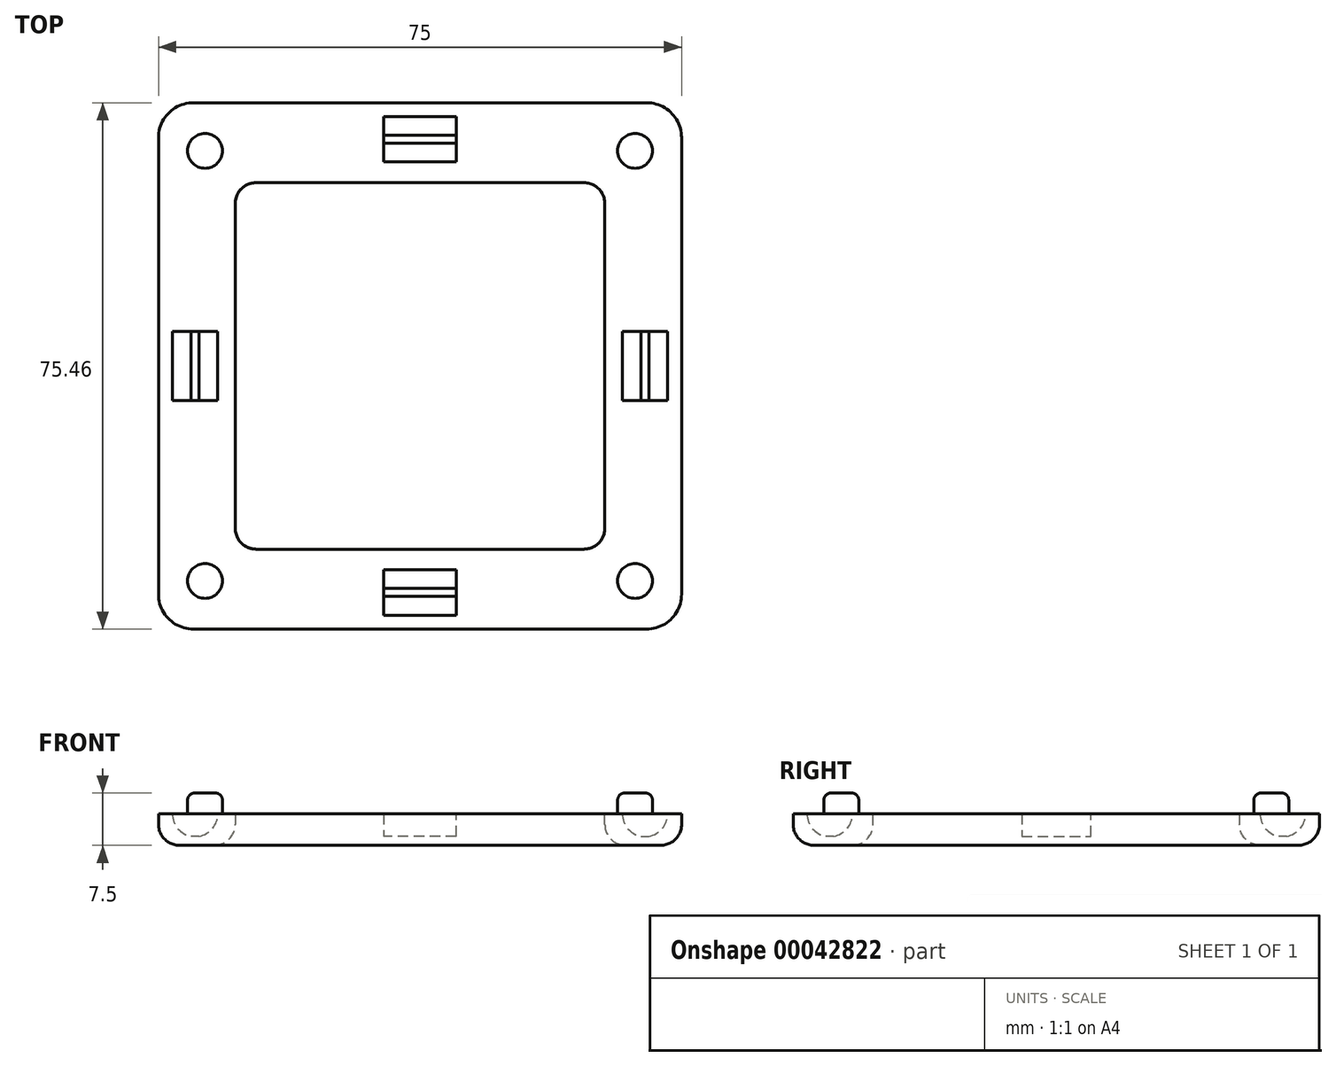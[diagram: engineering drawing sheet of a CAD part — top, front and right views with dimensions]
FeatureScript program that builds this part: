
annotation { "Feature Type Name" : "Feature", "Feature Type Description" : "" }
export const myFeature = defineFeature(function(context is Context, id is Id, definition is map)
    precondition{}
    {
        {
            var Q0;
            Q0=qCreatedBy(makeId("Top.planeOp"),FACE);
            var sketch = newSketch(context, id + "F0", { "sketchPlane" : qUnion([Q0])});
            skLineSegment(sketch, "E0", {"start": v(0, 37.27) * mm, "end": v(37.5, 37.27) * mm});
            skLineSegment(sketch, "E1", {"start": v(-37.5, 37.27) * mm, "end": v(0, 37.27) * mm});
            skLineSegment(sketch, "E2", {"start": v(-37.5, 37.27) * mm, "end": v(-37.5, -37.73) * mm});
            skLineSegment(sketch, "E3", {"start": v(-37.5, -37.73) * mm, "end": v(37.5, -37.73) * mm});
            skLineSegment(sketch, "E4", {"start": v(37.5, 37.27) * mm, "end": v(37.5, -0.23) * mm});
            skLineSegment(sketch, "E5", {"start": v(37.5, -0.23) * mm, "end": v(37.5, -37.73) * mm});
            skLineSegment(sketch, "E6", {"start": v(0, 26.27) * mm, "end": v(26.5, 26.27) * mm});
            skLineSegment(sketch, "E7", {"start": v(26.5, 26.27) * mm, "end": v(26.5, -26.73) * mm});
            skLineSegment(sketch, "E8", {"start": v(26.5, -26.73) * mm, "end": v(0, -26.73) * mm});
            skLineSegment(sketch, "E9", {"start": v(0, -26.73) * mm, "end": v(-26.5, -26.73) * mm});
            skLineSegment(sketch, "E10", {"start": v(-26.5, 26.27) * mm, "end": v(-26.5, 26.27) * mm});
            skLineSegment(sketch, "E11", {"start": v(0, 26.27) * mm, "end": v(-26.5, 26.27) * mm});
            skLineSegment(sketch, "E12", {"start": v(-26.5, 26.27) * mm, "end": v(-26.5, 0) * mm});
            skLineSegment(sketch, "E13", {"start": v(-26.5, -26.73) * mm, "end": v(-26.5, 0) * mm});
            skLineSegment(sketch, "E14", {"start": v(0, 0) * mm, "end": v(0, 26.27) * mm});
            skLineSegment(sketch, "E15", {"start": v(0, 0) * mm, "end": v(0, -26.73) * mm});
            skLineSegment(sketch, "E16", {"start": v(-26.5, 0) * mm, "end": v(0, 0) * mm});
            skLineSegment(sketch, "E17", {"start": v(0, 0) * mm, "end": v(26.5, -0.23) * mm});
            skLineSegment(sketch, "E18", {"start": v(0, -35.73) * mm, "end": v(5.2, -35.73) * mm});
            skLineSegment(sketch, "E19", {"start": v(-5.2, -35.73) * mm, "end": v(0, -35.73) * mm});
            skLineSegment(sketch, "E20", {"start": v(-5.2, -29.23) * mm, "end": v(-5.2, -35.73) * mm});
            skLineSegment(sketch, "E21", {"start": v(-5.2, -29.23) * mm, "end": v(5.2, -29.23) * mm});
            skLineSegment(sketch, "E22", {"start": v(5.2, -29.23) * mm, "end": v(5.2, -35.73) * mm});
            skLineSegment(sketch, "E23.MirrorCS", {"start": v(0, 35.73) * mm, "end": v(5.2, 35.73) * mm});
            skLineSegment(sketch, "E24.MirrorCS", {"start": v(-5.2, 29.23) * mm, "end": v(-5.2, 35.73) * mm});
            skLineSegment(sketch, "E25.MirrorCS", {"start": v(-5.2, 29.23) * mm, "end": v(5.2, 29.23) * mm});
            skLineSegment(sketch, "E26", {"start": v(5.2, 35.73) * mm, "end": v(5.2, 29.23) * mm});
            skLineSegment(sketch, "E27", {"start": v(0, 35.73) * mm, "end": v(-5.2, 35.73) * mm});
            skLineSegment(sketch, "E28", {"start": v(35.5, -0.23) * mm, "end": v(35.5, -5.43) * mm});
            skLineSegment(sketch, "E29", {"start": v(35.5, -5.43) * mm, "end": v(29, -5.43) * mm});
            skLineSegment(sketch, "E30", {"start": v(29, -5.43) * mm, "end": v(29, 4.97) * mm});
            skLineSegment(sketch, "E31", {"start": v(29, 4.97) * mm, "end": v(35.5, 4.97) * mm});
            skLineSegment(sketch, "E32", {"start": v(35.5, 4.97) * mm, "end": v(35.5, -0.23) * mm});
            skLineSegment(sketch, "E33.MirrorCS", {"start": v(-29, 4.97) * mm, "end": v(-35.5, 4.97) * mm});
            skLineSegment(sketch, "E34.MirrorCS", {"start": v(-29, -5.43) * mm, "end": v(-29, 4.97) * mm});
            skLineSegment(sketch, "E35.MirrorCS", {"start": v(-35.5, -5.43) * mm, "end": v(-29, -5.43) * mm});
            skLineSegment(sketch, "E36.MirrorCS", {"start": v(-35.5, -0.23) * mm, "end": v(-35.5, -5.43) * mm});
            skLineSegment(sketch, "E37.MirrorCS", {"start": v(-35.5, 4.97) * mm, "end": v(-35.5, -0.23) * mm});
            skSolve(sketch);
        }
        {
            var Q0;
            Q0=makeQuery(id+"F0.imprint","IMPRINT",FACE,{"disambiguationData":[TD([[makeQuery(id+"F0.imprint","IMPRINT",EDGE,{"derivedFrom":sQuery(id+"F0.wireOp",EDGE,"E18")}),1.0]])]});
            var Q1;
            Q1=makeQuery(id+"F0.imprint","IMPRINT",FACE,{"disambiguationData":[TD([[makeQuery(id+"F0.imprint","IMPRINT",EDGE,{"derivedFrom":sQuery(id+"F0.wireOp",EDGE,"E0")}),-1.0]])]});
            var Q2;
            {var subQ1=sQuery(id+"F0.wireOp",EDGE,"E8");Q2=makeQuery(id+"F0.imprint","IMPRINT",FACE,{"disambiguationData":[TD([[makeQuery(id+"F0.imprint","IMPRINT",EDGE,{"derivedFrom":subQ1}),-1.0]])]});}
            var Q3;
            Q3=makeQuery(id+"F0.imprint","IMPRINT",FACE,{"disambiguationData":[TD([[makeQuery(id+"F0.imprint","IMPRINT",EDGE,{"derivedFrom":sQuery(id+"F0.wireOp",EDGE,"E28")}),-1.0]])]});
            var Q4;
            Q4=makeQuery(id+"F0.imprint","IMPRINT",FACE,{"disambiguationData":[TD([[makeQuery(id+"F0.imprint","IMPRINT",EDGE,{"derivedFrom":sQuery(id+"F0.wireOp",EDGE,"E23.MirrorCS")}),-1.0]])]});
            var Q5;
            Q5=makeQuery(id+"F0.imprint","IMPRINT",FACE,{"disambiguationData":[TD([[makeQuery(id+"F0.imprint","IMPRINT",EDGE,{"derivedFrom":sQuery(id+"F0.wireOp",EDGE,"E9")}),-1.0]])]});
            var Q6;
            Q6=makeQuery(id+"F0.imprint","IMPRINT",FACE,{"disambiguationData":[TD([[makeQuery(id+"F0.imprint","IMPRINT",EDGE,{"derivedFrom":sQuery(id+"F0.wireOp",EDGE,"E11")}),1.0]])]});
            var Q7;
            {var subQ2=sQuery(id+"F0.wireOp",EDGE,"E6");Q7=makeQuery(id+"F0.imprint","IMPRINT",FACE,{"disambiguationData":[TD([[makeQuery(id+"F0.imprint","IMPRINT",EDGE,{"derivedFrom":subQ2}),-1.0]])]});}
            var Q8;
            Q8=makeQuery(id+"F0.imprint","IMPRINT",FACE,{"disambiguationData":[TD([[makeQuery(id+"F0.imprint","IMPRINT",EDGE,{"derivedFrom":sQuery(id+"F0.wireOp",EDGE,"E33.MirrorCS")}),1.0]])]});
            extrude(context, id + "F1", {"entities" : qUnion([Q0, Q1, Q2, Q3, Q4, Q5, Q6, Q7, Q8]), "oppositeDirection" : true, "depth" : 4.5 * mm});
        }
        {
            var Q0;
            {var subQ2=sQuery(id+"F0.wireOp",EDGE,"E6");Q0=makeQuery(id+"F0.imprint","IMPRINT",FACE,{"disambiguationData":[TD([[makeQuery(id+"F0.imprint","IMPRINT",EDGE,{"derivedFrom":subQ2}),-1.0]])]});}
            var Q1;
            {var subQ1=sQuery(id+"F0.wireOp",EDGE,"E8");Q1=makeQuery(id+"F0.imprint","IMPRINT",FACE,{"disambiguationData":[TD([[makeQuery(id+"F0.imprint","IMPRINT",EDGE,{"derivedFrom":subQ1}),-1.0]])]});}
            var Q2;
            Q2=makeQuery(id+"F0.imprint","IMPRINT",FACE,{"disambiguationData":[TD([[makeQuery(id+"F0.imprint","IMPRINT",EDGE,{"derivedFrom":sQuery(id+"F0.wireOp",EDGE,"E9")}),-1.0]])]});
            var Q3;
            Q3=makeQuery(id+"F0.imprint","IMPRINT",FACE,{"disambiguationData":[TD([[makeQuery(id+"F0.imprint","IMPRINT",EDGE,{"derivedFrom":sQuery(id+"F0.wireOp",EDGE,"E11")}),1.0]])]});
            extrude(context, id + "F2", {"entities" : qUnion([Q0, Q1, Q2, Q3]), "operationType" : NewBodyOperationType.REMOVE, "oppositeDirection" : true, "depth" : 5 * mm});
        }
        {
            var Q0;
            Q0=makeQuery(id+"F1.opExtrude","SWEPT_EDGE",EDGE,{"disambiguationData":[OSD([sQuery(id+"F0.wireOp",EDGE,"E3"),sQuery(id+"F0.wireOp",EDGE,"E5")])]});
            var Q1;
            Q1=makeQuery(id+"F1.opExtrude","SWEPT_EDGE",EDGE,{"disambiguationData":[OSD([sQuery(id+"F0.wireOp",EDGE,"E0"),sQuery(id+"F0.wireOp",EDGE,"E4")])]});
            var Q2;
            Q2=makeQuery(id+"F1.opExtrude","SWEPT_EDGE",EDGE,{"disambiguationData":[OSD([sQuery(id+"F0.wireOp",EDGE,"E2"),sQuery(id+"F0.wireOp",EDGE,"E3")])]});
            var Q3;
            Q3=makeQuery(id+"F1.opExtrude","SWEPT_EDGE",EDGE,{"disambiguationData":[OSD([sQuery(id+"F0.wireOp",EDGE,"E1"),sQuery(id+"F0.wireOp",EDGE,"E2")])]});
            fillet(context, id + "F3", {"entities" : qUnion([Q0, Q1, Q2, Q3]), "radius" : 5 * mm, "tangentPropagation" : true, "allowEdgeOverflow" : false});
        }
        {
            var Q0;
            Q0=makeQuery(id+"F2.boolean.opBoolean","COPY",EDGE,{"derivedFrom":makeQuery(id+"F2.opExtrude","SWEPT_EDGE",EDGE,{"disambiguationData":[OSD([sQuery(id+"F0.wireOp",EDGE,"E7"),sQuery(id+"F0.wireOp",EDGE,"E8")])]})});
            var Q1;
            Q1=makeQuery(id+"F2.boolean.opBoolean","COPY",EDGE,{"derivedFrom":makeQuery(id+"F2.opExtrude","SWEPT_EDGE",EDGE,{"disambiguationData":[OSD([sQuery(id+"F0.wireOp",EDGE,"E9"),sQuery(id+"F0.wireOp",EDGE,"E13")])]})});
            var Q2;
            Q2=makeQuery(id+"F2.boolean.opBoolean","COPY",EDGE,{"derivedFrom":makeQuery(id+"F2.opExtrude","SWEPT_EDGE",EDGE,{"disambiguationData":[OSD([sQuery(id+"F0.wireOp",EDGE,"E6"),sQuery(id+"F0.wireOp",EDGE,"E7")])]})});
            var Q3;
            Q3=makeQuery(id+"F2.boolean.opBoolean","COPY",EDGE,{"derivedFrom":makeQuery(id+"F2.opExtrude","SWEPT_EDGE",EDGE,{"disambiguationData":[OSD([sQuery(id+"F0.wireOp",EDGE,"E11"),sQuery(id+"F0.wireOp",EDGE,"E12")])]})});
            fillet(context, id + "F4", {"entities" : qUnion([Q0, Q1, Q2, Q3]), "radius" : 3 * mm, "tangentPropagation" : true, "allowEdgeOverflow" : false});
        }
        {
            var Q0;
            Q0=makeQuery(id+"F1.opExtrude","CAP_FACE",FACE,{"disambiguationData":[OSD([sQuery(id+"F0.wireOp",EDGE,"E0"),sQuery(id+"F0.wireOp",EDGE,"E1"),sQuery(id+"F0.wireOp",EDGE,"E2"),sQuery(id+"F0.wireOp",EDGE,"E3"),sQuery(id+"F0.wireOp",EDGE,"E4"),sQuery(id+"F0.wireOp",EDGE,"E5")])],"isStart":false});
            var Q1;
            Q1=makeQuery(id+"F1.opExtrude","CAP_EDGE",EDGE,{"disambiguationData":[OSD([sQuery(id+"F0.wireOp",EDGE,"E4"),sQuery(id+"F0.wireOp",EDGE,"E5")])],"isStart":false});
            var Q2;
            Q2=makeQuery(id+"F1.opExtrude","CAP_EDGE",EDGE,{"disambiguationData":[OSD([sQuery(id+"F0.wireOp",EDGE,"E2")])],"isStart":false});
            var Q3;
            {var subQ0=sQuery(id+"F0.wireOp",EDGE,"E2");var subQ1=sQuery(id+"F0.wireOp",EDGE,"E3");Q3=makeQuery(id+"F3.opFillet","BLEND_EDGE",EDGE,{"blendedFrom":[makeQuery(id+"F1.opExtrude","SWEPT_EDGE",EDGE,{"disambiguationData":[OSD([subQ0,subQ1])]}),makeQuery(id+"F1.opExtrude","CAP_FACE",FACE,{"disambiguationData":[OSD([sQuery(id+"F0.wireOp",EDGE,"E0"),sQuery(id+"F0.wireOp",EDGE,"E1"),subQ0,subQ1,sQuery(id+"F0.wireOp",EDGE,"E4"),sQuery(id+"F0.wireOp",EDGE,"E5")])],"isStart":false})],"blendedInto":[makeQuery(id+"F1.opExtrude","CAP_FACE",FACE,{"disambiguationData":[OSD([sQuery(id+"F0.wireOp",EDGE,"E0"),sQuery(id+"F0.wireOp",EDGE,"E1"),subQ0,subQ1,sQuery(id+"F0.wireOp",EDGE,"E4"),sQuery(id+"F0.wireOp",EDGE,"E5")])],"isStart":false})]});}
            var Q4;
            Q4=makeQuery(id+"F1.opExtrude","CAP_EDGE",EDGE,{"disambiguationData":[OSD([sQuery(id+"F0.wireOp",EDGE,"E3")])],"isStart":false});
            var Q5;
            Q5=makeQuery(id+"F1.opExtrude","CAP_EDGE",EDGE,{"disambiguationData":[OSD([sQuery(id+"F0.wireOp",EDGE,"E0"),sQuery(id+"F0.wireOp",EDGE,"E1")])],"isStart":false});
            var Q6;
            {var subQ0=sQuery(id+"F0.wireOp",EDGE,"E0");var subQ1=sQuery(id+"F0.wireOp",EDGE,"E4");Q6=makeQuery(id+"F3.opFillet","BLEND_EDGE",EDGE,{"blendedFrom":[makeQuery(id+"F1.opExtrude","SWEPT_EDGE",EDGE,{"disambiguationData":[OSD([subQ0,subQ1])]}),makeQuery(id+"F1.opExtrude","CAP_FACE",FACE,{"disambiguationData":[OSD([subQ0,sQuery(id+"F0.wireOp",EDGE,"E1"),sQuery(id+"F0.wireOp",EDGE,"E2"),sQuery(id+"F0.wireOp",EDGE,"E3"),subQ1,sQuery(id+"F0.wireOp",EDGE,"E5")])],"isStart":false})],"blendedInto":[makeQuery(id+"F1.opExtrude","CAP_FACE",FACE,{"disambiguationData":[OSD([subQ0,sQuery(id+"F0.wireOp",EDGE,"E1"),sQuery(id+"F0.wireOp",EDGE,"E2"),sQuery(id+"F0.wireOp",EDGE,"E3"),subQ1,sQuery(id+"F0.wireOp",EDGE,"E5")])],"isStart":false})]});}
            fillet(context, id + "F5", {"entities" : qUnion([Q0, Q1, Q2, Q3, Q4, Q5, Q6]), "radius" : 3 * mm, "allowEdgeOverflow" : false});
        }
        {
            var Q0;
            Q0=makeQuery(id+"F0.imprint","IMPRINT",FACE,{"disambiguationData":[TD([[makeQuery(id+"F0.imprint","IMPRINT",EDGE,{"derivedFrom":sQuery(id+"F0.wireOp",EDGE,"E18")}),1.0]])]});
            var Q1;
            Q1=makeQuery(id+"F0.imprint","IMPRINT",FACE,{"disambiguationData":[TD([[makeQuery(id+"F0.imprint","IMPRINT",EDGE,{"derivedFrom":sQuery(id+"F0.wireOp",EDGE,"E33.MirrorCS")}),1.0]])]});
            var Q2;
            Q2=makeQuery(id+"F0.imprint","IMPRINT",FACE,{"disambiguationData":[TD([[makeQuery(id+"F0.imprint","IMPRINT",EDGE,{"derivedFrom":sQuery(id+"F0.wireOp",EDGE,"E23.MirrorCS")}),-1.0]])]});
            var Q3;
            Q3=makeQuery(id+"F0.imprint","IMPRINT",FACE,{"disambiguationData":[TD([[makeQuery(id+"F0.imprint","IMPRINT",EDGE,{"derivedFrom":sQuery(id+"F0.wireOp",EDGE,"E28")}),-1.0]])]});
            extrude(context, id + "F6", {"entities" : qUnion([Q0, Q1, Q2, Q3]), "operationType" : NewBodyOperationType.REMOVE, "oppositeDirection" : true, "depth" : 3.2 * mm});
        }
        {
            var Q0;
            Q0=makeQuery(id+"F1.opExtrude","SWEPT_BODY",BODY,{"disambiguationData":[OSD([sQuery(id+"F0.wireOp",EDGE,"E0"),sQuery(id+"F0.wireOp",EDGE,"E1"),sQuery(id+"F0.wireOp",EDGE,"E2"),sQuery(id+"F0.wireOp",EDGE,"E3"),sQuery(id+"F0.wireOp",EDGE,"E4"),sQuery(id+"F0.wireOp",EDGE,"E5")])]});
            var Q1;
            Q1=qCreatedBy(makeId("Front.planeOp"),FACE);
            mirror(context, id + "F7", {"operationType" : NewBodyOperationType.ADD, "entities" : qUnion([Q0]), "mirrorPlane" : qUnion([Q1])});
        }
        {
            var Q0;
            Q0=makeQuery(id+"F6.boolean.opBoolean","COPY",FACE,{"derivedFrom":makeQuery(id+"F6.opExtrude","SWEPT_FACE",FACE,{"disambiguationData":[OSD([sQuery(id+"F0.wireOp",EDGE,"E33.MirrorCS")])]})});
            var sketch = newSketch(context, id + "F8", { "sketchPlane" : qUnion([Q0])});
            skArc(sketch, "E38", {"start": v(-35.5, 0) * mm, "mid": v(-32.25, -3.25) * mm, "end": v(-29, 0) * mm});
            skSolve(sketch);
        }
        {
            var Q0;
            {var subQ0=sQuery(id+"F0.wireOp",EDGE,"E33.MirrorCS");var subQ4=makeQuery(id+"F6.boolean.opBoolean","COPY",EDGE,{"derivedFrom":makeQuery(id+"F6.opExtrude","SWEPT_EDGE",EDGE,{"disambiguationData":[OSD([subQ0,sQuery(id+"F0.wireOp",EDGE,"E37.MirrorCS")])]})});Q0=makeQuery(id+"F8.imprint","IMPRINT",FACE,{"disambiguationData":[TD([[makeQuery(id+"F8.imprint","IMPRINT",EDGE,{"derivedFrom":subQ4}),-1.0]])]});}
            var Q1;
            {var subQ0=sQuery(id+"F0.wireOp",EDGE,"E33.MirrorCS");var subQ4=makeQuery(id+"F6.boolean.opBoolean","COPY",EDGE,{"derivedFrom":makeQuery(id+"F6.opExtrude","SWEPT_EDGE",EDGE,{"disambiguationData":[OSD([subQ0,sQuery(id+"F0.wireOp",EDGE,"E34.MirrorCS")])]})});Q1=makeQuery(id+"F8.imprint","IMPRINT",FACE,{"disambiguationData":[TD([[makeQuery(id+"F8.imprint","IMPRINT",EDGE,{"derivedFrom":subQ4}),1.0]])]});}
            extrude(context, id + "F9", {"entities" : qUnion([Q0, Q1]), "operationType" : NewBodyOperationType.ADD, "endBound" : BoundingType.UP_TO_NEXT, "depth" : 25 * mm});
        }
        {
            var Q0;
            Q0=makeQuery(id+"F1.opExtrude","SWEPT_BODY",BODY,{"disambiguationData":[OSD([sQuery(id+"F0.wireOp",EDGE,"E0"),sQuery(id+"F0.wireOp",EDGE,"E1"),sQuery(id+"F0.wireOp",EDGE,"E2"),sQuery(id+"F0.wireOp",EDGE,"E3"),sQuery(id+"F0.wireOp",EDGE,"E4"),sQuery(id+"F0.wireOp",EDGE,"E5")])]});
            var Q1;
            Q1=qCreatedBy(makeId("Right.planeOp"),FACE);
            mirror(context, id + "F10", {"operationType" : NewBodyOperationType.ADD, "entities" : qUnion([Q0]), "mirrorPlane" : qUnion([Q1])});
        }
        {
            var Q0;
            {var subQ0=makeQuery(id+"F1.opExtrude","CAP_FACE",FACE,{"disambiguationData":[OSD([sQuery(id+"F0.wireOp",EDGE,"E0"),sQuery(id+"F0.wireOp",EDGE,"E1"),sQuery(id+"F0.wireOp",EDGE,"E2"),sQuery(id+"F0.wireOp",EDGE,"E3"),sQuery(id+"F0.wireOp",EDGE,"E4"),sQuery(id+"F0.wireOp",EDGE,"E5")])],"isStart":true});Q0=makeQuery(id+"F7.boolean.opBoolean","MERGE",FACE,{"derivedFrom":[subQ0,makeQuery(id+"F7.opPattern","COPY",FACE,{"derivedFrom":subQ0,"instanceName":"1"})]});}
            var sketch = newSketch(context, id + "F11", { "sketchPlane" : qUnion([Q0])});
            skCircle(sketch, "E39", {"center": v(-30.83, 30.83) * mm, "radius": 2.5 * mm});
            skCircle(sketch, "E40", {"center": v(30.83, 30.83) * mm, "radius": 2.5 * mm});
            skCircle(sketch, "E41", {"center": v(30.83, -30.83) * mm, "radius": 2.5 * mm});
            skCircle(sketch, "E42", {"center": v(-30.83, -30.83) * mm, "radius": 2.5 * mm});
            skPoint(sketch, "E43.start.orphan", {"position": v(-25.62, 25.4) * mm});
            skPoint(sketch, "E44.orphan", {"position": v(-36.04, 36.27) * mm});
            skPoint(sketch, "E45.start.orphan", {"position": v(25.62, 25.4) * mm});
            skPoint(sketch, "E46.orphan", {"position": v(36.04, 36.27) * mm});
            skPoint(sketch, "E47.orphan", {"position": v(36.04, -36.27) * mm});
            skPoint(sketch, "E48.start.orphan", {"position": v(25.62, -25.4) * mm});
            skPoint(sketch, "E49.orphan", {"position": v(-25.62, -25.4) * mm});
            skPoint(sketch, "E50.end.orphan", {"position": v(-36.04, -36.27) * mm});
            skSolve(sketch);
        }
        {
            var Q0;
            Q0=makeQuery(id+"F11.imprint","IMPRINT",FACE,{"disambiguationData":[TD([[makeQuery(id+"F11.imprint","IMPRINT",EDGE,{"derivedFrom":sQuery(id+"F11.wireOp",EDGE,"E40")}),1.0]])]});
            var Q1;
            Q1=makeQuery(id+"F11.imprint","IMPRINT",FACE,{"disambiguationData":[TD([[makeQuery(id+"F11.imprint","IMPRINT",EDGE,{"derivedFrom":sQuery(id+"F11.wireOp",EDGE,"E41")}),1.0]])]});
            var Q2;
            Q2=makeQuery(id+"F11.imprint","IMPRINT",FACE,{"disambiguationData":[TD([[makeQuery(id+"F11.imprint","IMPRINT",EDGE,{"derivedFrom":sQuery(id+"F11.wireOp",EDGE,"E42")}),1.0]])]});
            var Q3;
            Q3=makeQuery(id+"F11.imprint","IMPRINT",FACE,{"disambiguationData":[TD([[makeQuery(id+"F11.imprint","IMPRINT",EDGE,{"derivedFrom":sQuery(id+"F11.wireOp",EDGE,"E39")}),1.0]])]});
            extrude(context, id + "F12", {"entities" : qUnion([Q0, Q1, Q2, Q3]), "operationType" : NewBodyOperationType.ADD, "depth" : 3 * mm});
        }
        {
            var Q0;
            Q0=makeQuery(id+"F12.opExtrude","CAP_EDGE",EDGE,{"disambiguationData":[OSD([sQuery(id+"F11.wireOp",EDGE,"E39")])],"isStart":false});
            var Q1;
            Q1=makeQuery(id+"F12.opExtrude","CAP_EDGE",EDGE,{"disambiguationData":[OSD([sQuery(id+"F11.wireOp",EDGE,"E40")])],"isStart":false});
            var Q2;
            Q2=makeQuery(id+"F12.opExtrude","CAP_EDGE",EDGE,{"disambiguationData":[OSD([sQuery(id+"F11.wireOp",EDGE,"E41")])],"isStart":false});
            var Q3;
            Q3=makeQuery(id+"F12.opExtrude","CAP_EDGE",EDGE,{"disambiguationData":[OSD([sQuery(id+"F11.wireOp",EDGE,"E42")])],"isStart":false});
            fillet(context, id + "F13", {"entities" : qUnion([Q0, Q1, Q2, Q3]), "radius" : 1 * mm, "tangentPropagation" : true, "allowEdgeOverflow" : false});
        }
        {
            var Q0;
            Q0=makeQuery(id+"F1.opExtrude","SWEPT_BODY",BODY,{"disambiguationData":[OSD([sQuery(id+"F0.wireOp",EDGE,"E0"),sQuery(id+"F0.wireOp",EDGE,"E1"),sQuery(id+"F0.wireOp",EDGE,"E2"),sQuery(id+"F0.wireOp",EDGE,"E3"),sQuery(id+"F0.wireOp",EDGE,"E4"),sQuery(id+"F0.wireOp",EDGE,"E5")])]});
            transform(context, id + "F14", {"entities" : qUnion([Q0]), "transformType" : TransformType.TRANSLATION_3D, "dx" : 0 * mm, "dy" : 0 * mm, "dz" : 0 * mm, "makeCopy" : true});
        }
        {
            var Q0;
            Q0=makeQuery(id+"F14.opPattern","COPY",BODY,{"derivedFrom":makeQuery(id+"F1.opExtrude","SWEPT_BODY",BODY,{"disambiguationData":[OSD([sQuery(id+"F0.wireOp",EDGE,"E0"),sQuery(id+"F0.wireOp",EDGE,"E1"),sQuery(id+"F0.wireOp",EDGE,"E2"),sQuery(id+"F0.wireOp",EDGE,"E3"),sQuery(id+"F0.wireOp",EDGE,"E4"),sQuery(id+"F0.wireOp",EDGE,"E5")])]}),"instanceName":"1"});
            transform(context, id + "F15", {"entities" : qUnion([Q0]), "transformType" : TransformType.TRANSLATION_3D, "dx" : 0 * mm, "dy" : 0 * mm, "dz" : 0 * mm, "makeCopy" : true});
        }
        {
            var Q0;
            Q0=makeQuery(id+"F14.opPattern","COPY",BODY,{"derivedFrom":makeQuery(id+"F1.opExtrude","SWEPT_BODY",BODY,{"disambiguationData":[OSD([sQuery(id+"F0.wireOp",EDGE,"E0"),sQuery(id+"F0.wireOp",EDGE,"E1"),sQuery(id+"F0.wireOp",EDGE,"E2"),sQuery(id+"F0.wireOp",EDGE,"E3"),sQuery(id+"F0.wireOp",EDGE,"E4"),sQuery(id+"F0.wireOp",EDGE,"E5")])]}),"instanceName":"1"});
            deleteBodies(context, id + "F16", {"entities" : qUnion([Q0])});
        }
        {
            var Q0;
            Q0=makeQuery(id+"F15.opPattern","COPY",BODY,{"derivedFrom":makeQuery(id+"F14.opPattern","COPY",BODY,{"derivedFrom":makeQuery(id+"F1.opExtrude","SWEPT_BODY",BODY,{"disambiguationData":[OSD([sQuery(id+"F0.wireOp",EDGE,"E0"),sQuery(id+"F0.wireOp",EDGE,"E1"),sQuery(id+"F0.wireOp",EDGE,"E2"),sQuery(id+"F0.wireOp",EDGE,"E3"),sQuery(id+"F0.wireOp",EDGE,"E4"),sQuery(id+"F0.wireOp",EDGE,"E5")])]}),"instanceName":"1"}),"instanceName":"1"});
            deleteBodies(context, id + "F17", {"entities" : qUnion([Q0])});
        }
        {
            var Q0;
            Q0=makeQuery(id+"F6.boolean.opBoolean","COPY",FACE,{"derivedFrom":makeQuery(id+"F6.opExtrude","SWEPT_FACE",FACE,{"disambiguationData":[OSD([sQuery(id+"F0.wireOp",EDGE,"E20")])]})});
            var sketch = newSketch(context, id + "F18", { "sketchPlane" : qUnion([Q0])});
            skArc(sketch, "E51", {"start": v(-35.73, 0) * mm, "mid": v(-32.48, -3.25) * mm, "end": v(-29.23, 0) * mm});
            skSolve(sketch);
        }
        {
            var Q0;
            Q0=makeQuery(id+"F6.boolean.opBoolean","COPY",FACE,{"derivedFrom":makeQuery(id+"F6.opExtrude","SWEPT_FACE",FACE,{"disambiguationData":[OSD([sQuery(id+"F0.wireOp",EDGE,"E24.MirrorCS")])]})});
            var sketch = newSketch(context, id + "F19", { "sketchPlane" : qUnion([Q0])});
            skArc(sketch, "E52", {"start": v(29.23, 0) * mm, "mid": v(32.48, -3.25) * mm, "end": v(35.73, 0) * mm});
            skSolve(sketch);
        }
        {
            var Q0;
            {var subQ0=sQuery(id+"F0.wireOp",EDGE,"E20");var subQ4=makeQuery(id+"F6.boolean.opBoolean","COPY",EDGE,{"derivedFrom":makeQuery(id+"F6.opExtrude","SWEPT_EDGE",EDGE,{"disambiguationData":[OSD([sQuery(id+"F0.wireOp",EDGE,"E19"),subQ0])]})});Q0=makeQuery(id+"F18.imprint","IMPRINT",FACE,{"disambiguationData":[TD([[makeQuery(id+"F18.imprint","IMPRINT",EDGE,{"derivedFrom":subQ4}),-1.0]])]});}
            var Q1;
            {var subQ0=sQuery(id+"F0.wireOp",EDGE,"E20");var subQ4=makeQuery(id+"F6.boolean.opBoolean","COPY",EDGE,{"derivedFrom":makeQuery(id+"F6.opExtrude","SWEPT_EDGE",EDGE,{"disambiguationData":[OSD([subQ0,sQuery(id+"F0.wireOp",EDGE,"E21")])]})});Q1=makeQuery(id+"F18.imprint","IMPRINT",FACE,{"disambiguationData":[TD([[makeQuery(id+"F18.imprint","IMPRINT",EDGE,{"derivedFrom":subQ4}),1.0]])]});}
            var Q2;
            {var subQ0=sQuery(id+"F0.wireOp",EDGE,"E24.MirrorCS");var subQ4=makeQuery(id+"F6.boolean.opBoolean","COPY",EDGE,{"derivedFrom":makeQuery(id+"F6.opExtrude","SWEPT_EDGE",EDGE,{"disambiguationData":[OSD([subQ0,sQuery(id+"F0.wireOp",EDGE,"E25.MirrorCS")])]})});Q2=makeQuery(id+"F19.imprint","IMPRINT",FACE,{"disambiguationData":[TD([[makeQuery(id+"F19.imprint","IMPRINT",EDGE,{"derivedFrom":subQ4}),-1.0]])]});}
            var Q3;
            {var subQ0=sQuery(id+"F0.wireOp",EDGE,"E24.MirrorCS");var subQ1=makeQuery(id+"F6.boolean.opBoolean","COPY",EDGE,{"derivedFrom":makeQuery(id+"F6.opExtrude","SWEPT_EDGE",EDGE,{"disambiguationData":[OSD([subQ0,sQuery(id+"F0.wireOp",EDGE,"E27")])]})});Q3=makeQuery(id+"F19.imprint","IMPRINT",FACE,{"disambiguationData":[TD([[makeQuery(id+"F19.imprint","IMPRINT",EDGE,{"derivedFrom":subQ1}),1.0]])]});}
            extrude(context, id + "F20", {"entities" : qUnion([Q0, Q1, Q2, Q3]), "operationType" : NewBodyOperationType.ADD, "endBound" : BoundingType.UP_TO_NEXT, "depth" : 25 * mm});
        }
    });
